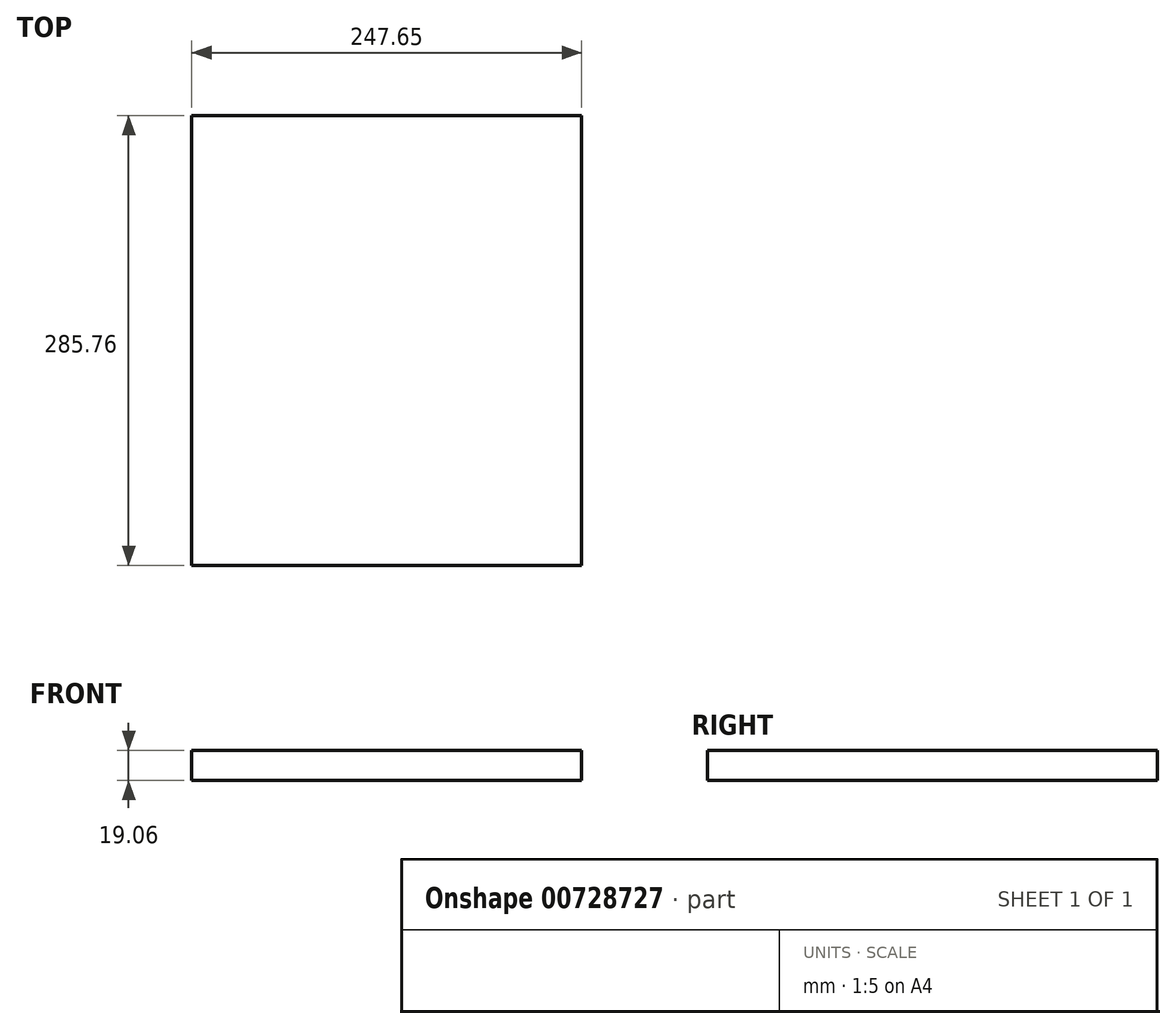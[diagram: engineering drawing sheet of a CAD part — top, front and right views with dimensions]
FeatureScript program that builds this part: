
annotation { "Feature Type Name" : "Feature", "Feature Type Description" : "" }
export const myFeature = defineFeature(function(context is Context, id is Id, definition is map)
    precondition{}
    {
        {
            var Q0;
            Q0=qCreatedBy(makeId("Right.planeOp"),FACE);
            var sketch = newSketch(context, id + "F0", { "sketchPlane" : qUnion([Q0])});
            skLineSegment(sketch, "E0.bottom", {"start": v(142.88, 9.53) * mm, "end": v(-142.88, 9.53) * mm});
            skLineSegment(sketch, "E0.top", {"start": v(142.88, -9.53) * mm, "end": v(-142.87, -9.53) * mm});
            skLineSegment(sketch, "E0.left", {"start": v(142.88, 9.53) * mm, "end": v(142.88, -9.53) * mm});
            skLineSegment(sketch, "E0.right", {"start": v(-142.88, 9.53) * mm, "end": v(-142.88, -9.53) * mm});
            skPoint(sketch, "E0.middle", {"position": v(0, 0) * mm});
            skSolve(sketch);
        }
        {
            var Q0;
            Q0 = qSketchRegion(id + "F0", true);
            extrude(context, id + "F1", {"entities" : qUnion([Q0]), "depth" : 247.65 * mm, "offsetDistance" : 25.4 * mm});
        }
    });
